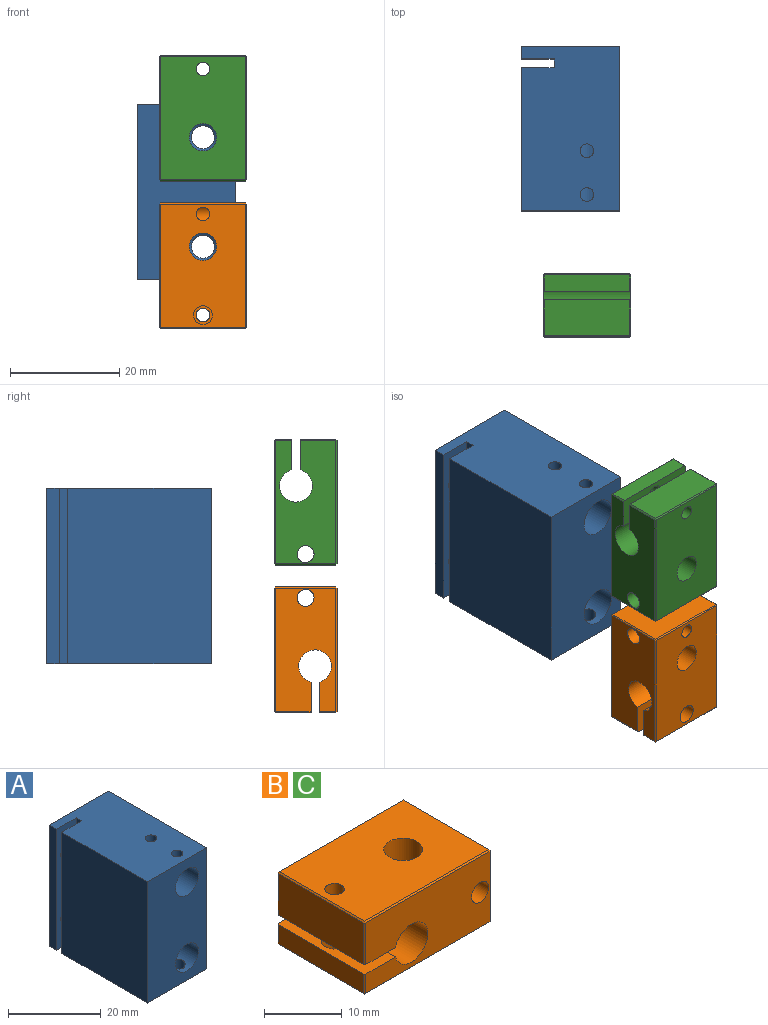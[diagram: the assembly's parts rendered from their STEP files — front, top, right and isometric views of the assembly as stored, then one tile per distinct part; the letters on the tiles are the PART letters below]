
ASSEMBLY  parts=3 mates=2
PART A: 38 faces, bbox 18x30x32 mm
  f0: plane 32x26.2mm, normal (-1,0,0), area 838.4mm2, adj f1,f2,f12,f33
  f1: plane 30x18mm, normal (0,0,1), area 520.6mm2, adj f0,f8,f9,f10,f11,f12,f13,f31
  f2: plane 30x18mm, normal (0,0,-1), area 512.2mm2, adj f0,f10,f11,f12,f13,f29,f30,f31
  f3: cylinder r=1.7mm len=3.4mm, axis (0,1,0), area 23.5mm2, adj f10,f32
  f4: cylinder r=1.7mm len=3.4mm, axis (0,1,0), area 23.5mm2, adj f10,f32
  f5: cylinder r=3.5mm len=13mm, axis (0,-1,0), area 267.1mm2, adj f12,f20,f29,f30
  f6: cylinder r=2.1mm len=9.02mm, axis (0,-1,0), area 119mm2, adj f21,f23
  f7: cylinder r=2.1mm len=9.02mm, axis (0,-1,0), area 119mm2, adj f20,f25
  f8: cylinder r=1.25mm len=2.73mm, axis (0,0,1), area 20.5mm2, adj f1,f22
  f9: cylinder r=1.25mm len=2.73mm, axis (0,0,1), area 20.5mm2, adj f1,f22
  f10: plane 32x18mm, normal (0,1,0), area 448.2mm2, adj f1,f2,f3,f4,f11,f13,f24,f26
  f11: plane 32x2.2mm, normal (-1,0,0), area 70.4mm2, adj f1,f2,f10,f32
  f12: plane 32x18mm, normal (0,-1,0), area 499mm2, adj f0,f1,f2,f5,f13,f22
  f13: plane 32x30mm, normal (1,0,0), area 945.3mm2, adj f1,f2,f10,f12,f15,f17,f19
  f14: cone r=0mm half-angle=59deg, axis (1,0,0), area 5.7mm2, adj f15
  f15: cylinder r=1.25mm len=7.5mm, axis (1,0,0), area 58.9mm2, adj f13,f14
  f16: cone r=0mm half-angle=59deg, axis (1,0,0), area 5.7mm2, adj f17
  f17: cylinder r=1.25mm len=7.5mm, axis (1,0,0), area 58.9mm2, adj f13,f16
  f18: cone r=0mm half-angle=59deg, axis (1,0,0), area 5.7mm2, adj f19
  f19: cylinder r=1.25mm len=7.5mm, axis (1,0,0), area 58.9mm2, adj f13,f18
  f20: cone r=0mm half-angle=59deg, axis (0,-1,0), area 28.7mm2, adj f5,f7
  f21: cone r=0mm half-angle=59deg, axis (0,-1,0), area 28.7mm2, adj f6,f22
  f22: cylinder r=3.5mm len=13mm, axis (0,-1,0), area 275.9mm2, adj f8,f9,f12,f21
  f23: cone r=0mm half-angle=59deg, axis (0,1,0), area 42.5mm2, adj f6,f24
  f24: cylinder r=4mm len=8mm, axis (0,1,0), area 150.8mm2, adj f10,f23
  f25: cone r=0mm half-angle=59deg, axis (0,1,0), area 42.5mm2, adj f7,f26
  f26: cylinder r=4mm len=8mm, axis (0,1,0), area 150.8mm2, adj f10,f25
  f27: cone r=0mm half-angle=59deg, axis (0,1,0), area 10.6mm2, adj f28
  f28: cylinder r=1.7mm len=5mm, axis (0,1,0), area 53.4mm2, adj f10,f27
  f29: cylinder r=1.7mm len=3.4mm, axis (0,0,-1), area 29mm2, adj f2,f5
  f30: cylinder r=1.7mm len=3.4mm, axis (0,0,-1), area 29mm2, adj f2,f5
  f31: plane 32x1.6mm, normal (-1,0,0), area 51.2mm2, adj f1,f2,f32,f33
  f32: plane 32x6mm, normal (0,-1,0), area 173.9mm2, adj f1,f2,f3,f4,f11,f31
  f33: plane 32x6mm, normal (0,1,0), area 173.9mm2, adj f0,f1,f2,f31,f35,f37
  f34: cone r=0mm half-angle=59deg, axis (0,1,0), area 10.6mm2, adj f35
  f35: cylinder r=1.7mm len=3.4mm, axis (0,1,0), area 12.8mm2, adj f33,f34
  f36: cone r=0mm half-angle=59deg, axis (0,1,0), area 10.6mm2, adj f37
  f37: cylinder r=1.7mm len=3.4mm, axis (0,1,0), area 12.8mm2, adj f33,f36
PART B: 37 faces, bbox 23x16x11.5 mm
  f0: cylinder r=1.55mm len=16mm, axis (0,-1,0), area 150.4mm2, adj f2,f4,f13
  f1: plane 15.6x3.05mm, normal (-1,0,0), area 47.6mm2, adj f9,f27,f33,f36
  f2: plane 22.6x11.1mm, normal (0,1,0), area 207mm2, adj f0,f8,f9,f10,f19,f24,f30,f34
  f3: plane 15.6x6.55mm, normal (-1,0,0), area 102.2mm2, adj f8,f15,f18,f19
  f4: plane 22.6x11.1mm, normal (0,-1,0), area 207mm2, adj f0,f8,f9,f10,f15,f17,f22,f27
  f5: plane 15.6x11.1mm, normal (1,0,0), area 173.2mm2, adj f22,f23,f29,f30
  f6: plane 22.6x15.6mm, normal (0,0,1), area 328mm2, adj f11,f12,f17,f18,f23,f24
  f7: plane 22.6x15.6mm, normal (0,0,-1), area 318.9mm2, adj f12,f13,f14,f28,f29,f33,f34
  f8: plane 16x5.6mm, normal (0,0,-1), area 84.6mm2, adj f2,f3,f4,f10,f11,f15,f19
  f9: plane 16x5.6mm, normal (0,0,1), area 80.4mm2, adj f1,f2,f4,f10,f14,f27,f36
  f10: cylinder r=3mm len=16mm, axis (0,-1,0), area 277.3mm2, adj f2,f4,f8,f9
  f11: cylinder r=1.25mm len=6.75mm, axis (0,0,1), area 53mm2, adj f6,f8
  f12: cylinder r=2.5mm len=11.5mm, axis (0,0,1), area 180.6mm2, adj f6,f7
  f13: cylinder r=1.25mm len=4.83mm, axis (0,0,-1), area 35.3mm2, adj f0,f7
  f14: cylinder r=1.7mm len=3.4mm, axis (0,0,-1), area 34.7mm2, adj f7,f9
  f15: plane 6.55x0.2mm, normal (-0.71,-0.71,0), area 1.9mm2, adj f3,f4,f8,f16
  f16: plane 0.2x0.2mm, normal (-0.58,-0.58,0.58), area 0mm2, adj f15,f17,f18
  f17: plane 22.6x0.2mm, normal (0,-0.71,0.71), area 6.4mm2, adj f4,f6,f16,f20
  f18: plane 15.6x0.2mm, normal (-0.71,0,0.71), area 4.4mm2, adj f3,f6,f16,f21
  f19: plane 6.55x0.2mm, normal (-0.71,0.71,0), area 1.9mm2, adj f2,f3,f8,f21
  f20: plane 0.2x0.2mm, normal (0.58,-0.58,0.58), area 0mm2, adj f17,f22,f23
  f21: plane 0.2x0.2mm, normal (-0.58,0.58,0.58), area 0mm2, adj f18,f19,f24
  f22: plane 11.1x0.2mm, normal (0.71,-0.71,0), area 3.1mm2, adj f4,f5,f20,f25
  f23: plane 15.6x0.2mm, normal (0.71,0,0.71), area 4.4mm2, adj f5,f6,f20,f26
  f24: plane 22.6x0.2mm, normal (0,0.71,0.71), area 6.4mm2, adj f2,f6,f21,f26
  f25: plane 0.2x0.2mm, normal (0.58,-0.58,-0.58), area 0mm2, adj f22,f28,f29
  f26: plane 0.2x0.2mm, normal (0.58,0.58,0.58), area 0mm2, adj f23,f24,f30
  f27: plane 3.05x0.2mm, normal (-0.71,-0.71,0), area 0.9mm2, adj f1,f4,f9,f31
  f28: plane 22.6x0.2mm, normal (0,-0.71,-0.71), area 6.4mm2, adj f4,f7,f25,f31
  f29: plane 15.6x0.2mm, normal (0.71,0,-0.71), area 4.4mm2, adj f5,f7,f25,f32
  f30: plane 11.1x0.2mm, normal (0.71,0.71,0), area 3.1mm2, adj f2,f5,f26,f32
  f31: plane 0.2x0.2mm, normal (-0.58,-0.58,-0.58), area 0mm2, adj f27,f28,f33
  f32: plane 0.2x0.2mm, normal (0.58,0.58,-0.58), area 0mm2, adj f29,f30,f34
  f33: plane 15.6x0.2mm, normal (-0.71,0,-0.71), area 4.4mm2, adj f1,f7,f31,f35
  f34: plane 22.6x0.2mm, normal (0,0.71,-0.71), area 6.4mm2, adj f2,f7,f32,f35
  f35: plane 0.2x0.2mm, normal (-0.58,0.58,-0.58), area 0mm2, adj f33,f34,f36
  f36: plane 3.05x0.2mm, normal (-0.71,0.71,0), area 0.9mm2, adj f1,f2,f9,f35
PART C: same geometry as B
PLACE A t=(-16.18,-8.75,14.21)mm
PLACE B rot(axis=(-0.58,-0.58,-0.58),120deg) t=(33.74,-50.31,8.12)mm
PLACE C rot(axis=(0.58,0.58,-0.58),120deg) t=(33.74,-38.81,52.29)mm
MATE planar C.f12 <-> A.f6  axis (0,1,0) through (27.95,-38.81,40.21)mm
MATE planar A.f5 <-> B.f12  axis (0,-1,0) through (27.95,-27.31,20.21)mm
